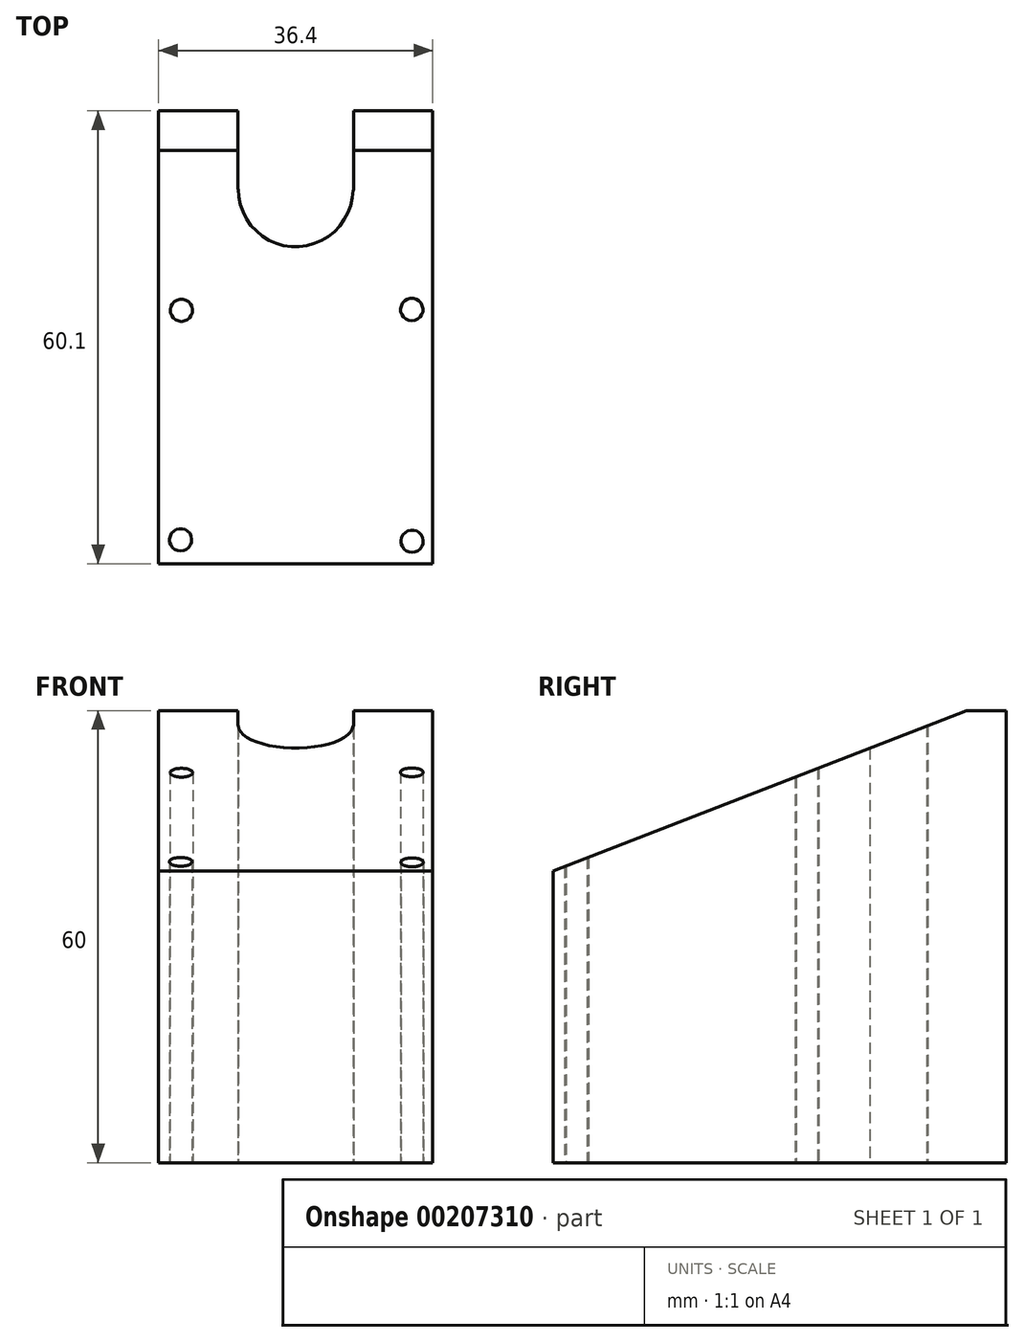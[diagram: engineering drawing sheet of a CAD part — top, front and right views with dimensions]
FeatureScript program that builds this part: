
annotation { "Feature Type Name" : "Feature", "Feature Type Description" : "" }
export const myFeature = defineFeature(function(context is Context, id is Id, definition is map)
    precondition{}
    {
        {
            var Q0;
            Q0=qCreatedBy(makeId("Top.planeOp"),FACE);
            var sketch = newSketch(context, id + "F0", { "sketchPlane" : qUnion([Q0])});
            skLineSegment(sketch, "E0.bottom", {"start": v(41.16, 10) * mm, "end": v(41.26, 10) * mm});
            skLineSegment(sketch, "E0.top", {"start": v(4.76, -26.5) * mm, "end": v(41.26, -26.5) * mm});
            skLineSegment(sketch, "E0.left", {"start": v(4.76, 10) * mm, "end": v(4.76, -26.5) * mm});
            skLineSegment(sketch, "E0.right", {"start": v(41.26, 10) * mm, "end": v(41.26, -26.5) * mm});
            skCircle(sketch, "E1", {"center": v(7.8, 7.11) * mm, "radius": 1.5 * mm});
            skCircle(sketch, "E2", {"center": v(38.37, 7.23) * mm, "radius": 1.5 * mm});
            skCircle(sketch, "E3", {"center": v(7.7, -23.35) * mm, "radius": 1.5 * mm});
            skCircle(sketch, "E4", {"center": v(38.41, -23.53) * mm, "radius": 1.5 * mm});
            skLineSegment(sketch, "E5.bottom", {"start": v(4.76, -26.5) * mm, "end": v(41.16, -26.5) * mm});
            skLineSegment(sketch, "E5.top", {"start": v(4.76, 33.6) * mm, "end": v(15.26, 33.6) * mm});
            skLineSegment(sketch, "E5.left", {"start": v(4.76, -26.5) * mm, "end": v(4.76, 33.6) * mm});
            skLineSegment(sketch, "E5.right", {"start": v(41.16, -26.5) * mm, "end": v(41.16, 33.6) * mm});
            skLineSegment(sketch, "E6", {"start": v(30.66, 33.6) * mm, "end": v(41.16, 33.6) * mm});
            skLineSegment(sketch, "E7", {"start": v(15.26, 33.6) * mm, "end": v(15.26, 23.21) * mm});
            skLineSegment(sketch, "E8", {"start": v(30.66, 33.6) * mm, "end": v(30.66, 23.1) * mm});
            skLineSegment(sketch, "E9", {"start": v(30.66, 23.1) * mm, "end": v(30.59, 23.1) * mm});
            skArc(sketch, "E10", {"start": v(15.33, 23.21) * mm, "mid": v(22.9, 15.52) * mm, "end": v(30.59, 23.1) * mm});
            skLineSegment(sketch, "E11.trimOffspring", {"start": v(15.33, 23.21) * mm, "end": v(15.26, 23.21) * mm});
            skSolve(sketch);
        }
        {
            var Q0;
            Q0=makeQuery(id+"F0.imprint","IMPRINT",FACE,{"disambiguationData":[TD([[makeQuery(id+"F0.imprint","IMPRINT",EDGE,{"derivedFrom":sQuery(id+"F0.wireOp",EDGE,"E1")}),-1.0]])]});
            extrude(context, id + "F1", {"entities" : qUnion([Q0]), "depth" : 60 * mm});
        }
        {
            var Q0;
            Q0=makeQuery(id+"F1.opExtrude","SWEPT_FACE",FACE,{"disambiguationData":[OSD([sQuery(id+"F0.wireOp",EDGE,"E5.left")])]});
            var sketch = newSketch(context, id + "F2", { "sketchPlane" : qUnion([Q0])});
            skLineSegment(sketch, "E12", {"start": v(-28.34, 60) * mm, "end": v(26.5, 38.7) * mm});
            skLineSegment(sketch, "E13.bottom", {"start": v(2.02, 27.61) * mm, "end": v(12.02, 27.61) * mm});
            skLineSegment(sketch, "E13.top", {"start": v(2.02, 20.61) * mm, "end": v(12.02, 20.61) * mm});
            skLineSegment(sketch, "E13.left", {"start": v(2.02, 27.61) * mm, "end": v(2.02, 20.61) * mm});
            skLineSegment(sketch, "E13.right", {"start": v(12.02, 27.61) * mm, "end": v(12.02, 20.61) * mm});
            skSolve(sketch);
        }
        {
            var Q0;
            {var subQ0=sQuery(id+"F2.wireOp",EDGE,"E12");Q0=makeQuery(id+"F2.imprint","IMPRINT",FACE,{"disambiguationData":[TD([[makeQuery(id+"F2.imprint","IMPRINT",EDGE,{"derivedFrom":subQ0}),1.0]])]});}
            extrude(context, id + "F3", {"entities" : qUnion([Q0]), "operationType" : NewBodyOperationType.REMOVE, "endBound" : BoundingType.THROUGH_ALL, "oppositeDirection" : true, "depth" : 25 * mm});
        }
    });
